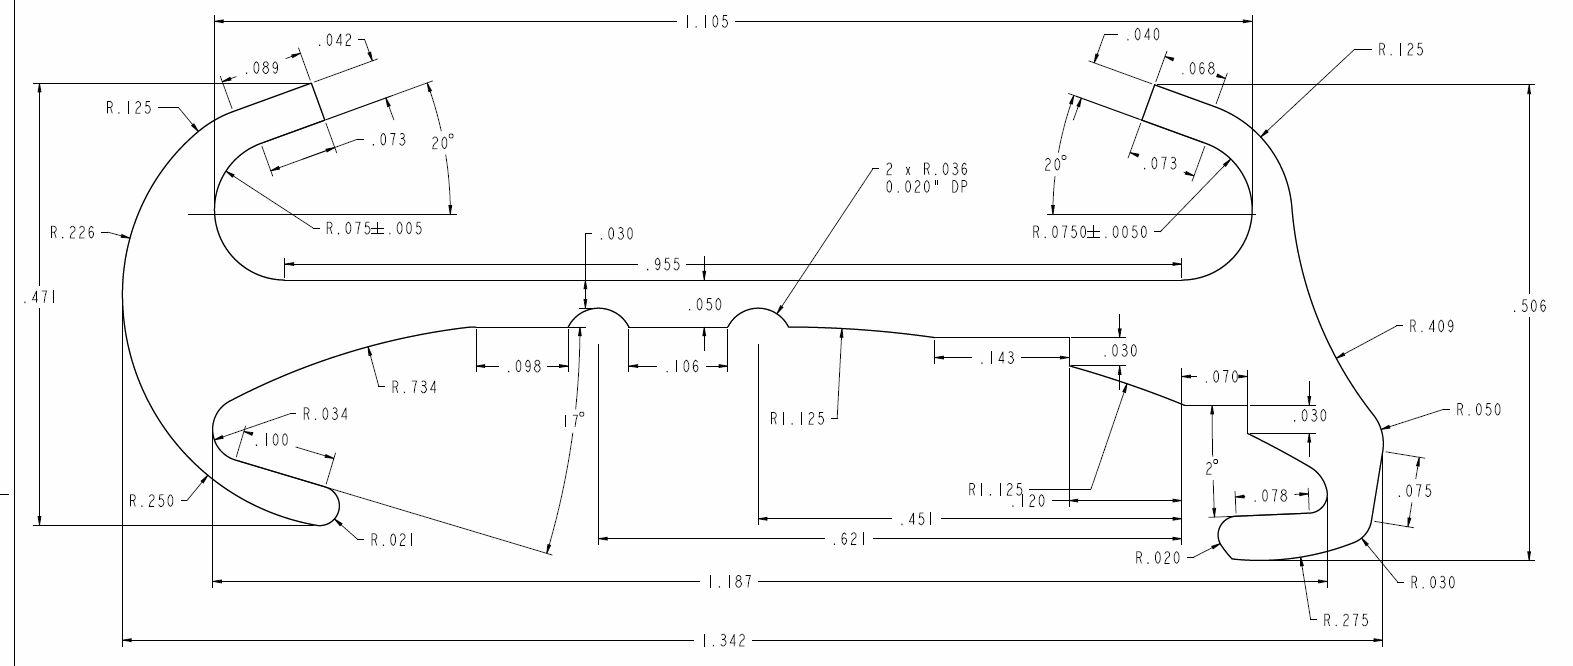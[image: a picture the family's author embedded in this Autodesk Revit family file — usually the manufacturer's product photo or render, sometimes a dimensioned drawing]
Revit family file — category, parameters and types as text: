
# Revit family: ONRZH 5.125'' Heated only-All
name_source: partatom
category: Mechanical Equipment
units: mm (PartAtom-declared; Revit-internal decimal feet)

## family parameters
Always vertical = Yes
Cut with Voids When Loaded = No
OmniClass Number = 23.40.40.11.17
OmniClass Title = Refrigerated Cases
Part Type = Normal
Room Calculation Point = No
Round Connector Dimension = Use Radius
Shared = No
Work Plane-Based = Yes

## types (6) — shared parameters
22" Shelf = Yes
ANTI CON AMPS = 4 A
BASE = BLACK
Certifications = NSF 7, UL471, CSA
DATE = 02/08/2016
DEFROST AMPS = 26 A
DESIGNERS NAME = SHIDDRAMESH
DISCHARGE AIR TEMP. = -8 °F
DISCHARGE AIR VELOCITY = 350 FPM
DRAIN HEATERS AMPS = 3 A
Default Elevation = 48"
Defrost Num Day = 4
Defrost Termination = 50 °F
Defrost Type = ELECTRIC DEFROST
Defrosts Per Day_2 = 1
Description = High Narrow Back-to-Back Reach-In Glass Door Merchandiser
Discharge Air Velocity (FPM) = 350
Door Type = Heated
EQUIPMENT DESCRIPTION = High Narrow Back-to-Back Reach-In Glass Door Merchandiser
EQUIPMENT MARK = ONRZH
Electric Defrost Fail-Safe = 46
Electric Defrost Run-Off Time (Min) = 0
Electric Defrost Termination = 50
Evap Temp = -15
HIGH EFFICIENCY FANS AMPS = 1 A
Height = 85 1/4"
Hot Gas Defrost Fail-Safe = 24
Hot Gas Defrost Run-Off Time (Min) = 13-15
Hot Gas Defrost Termination = 73
Item Description = High Narrow Back-to-Back Reach-In Glass Door Merchandiser
LIGHT AMPS = 1 A
Legend Number = ONRZH
Load Mbh = 1.06
Manufacturer = HILL PHOENIX
Model = ONRZH
POWER FACTOR = 1
Painted Metal Exterior = CHARCOAL BROWN
REFRIGERATION PIPING = COPPER PIPE
Refrig Charge Lbs = 0
Superheat Set Point @ Bulb (F) = 3-5
URL = http://www.hillphoenix.com
Width = 67 1/8"
length = Yes

## per-type parameters (varying)
- 2- Door Frozen Food: 101-LE DOOR FRAME AMPS=1 A; 101-LE DOOR FRAME WATTS=151 W; 208 Amps SSD Defrost Phase 1=7.5; 208 Watts SSD Defrost Phase 1=1552; 240 Amps SSD Defrost  Phase 1=8.6; 240 Watts SSD Defrost Phase 1=2068; 3 Phase SSD Defrost 208 Amps=6.5; 3 Phase SSD Defrost 208 Watts=1552; 3 Phase SSD Defrost 240 Amps=7.5; 3 Phase SSD Defrost 240 Watts=2068; Application Discipline=Frozen; BTUH Conventional=910; BTUH Parallel=895; CENTER LINE & DRAIN=30"; DOOR CONFIGURATION=MASTER DOOR : 30" X 68 3/8" 2 DOOR A SWING (LEFT OPENING); Discharge Air (F)=-1; Evaportator (F)=-7; GE Immersion Amps=0 A; GE Immersion Watts=41 W; Heated Doors Amps=0.78; Heated Doors Watts=67; Heated Option Amps=2.04; Heated Option Watts=219; Length=60"; Low E Doors Amps=0.34; Low E Doors Watts=41; Low E Rails Amps=1.6; Low E Rails Watts=192; Optimax Pro Amps=0 A; Optimax Pro Watts=43 W; SSD Fans Per Case=2; SSD High Efficiency Amps=0.6; SSD High Efficiency Fan Watts=50; SSD Tank Heater Amps=1.6; SSD Tank Heater Watts=152
- 3-Door Frozen Food: 101-LE DOOR FRAME AMPS=2 A; 101-LE DOOR FRAME WATTS=211 W; 208 Amps SSD Defrost Phase 1=10.9; 208 Watts SSD Defrost Phase 1=2274; 240 Amps SSD Defrost  Phase 1=12.6; 240 Watts SSD Defrost Phase 1=3018; 3 Phase SSD Defrost 208 Amps=9.5; 3 Phase SSD Defrost 208 Watts=2274; 3 Phase SSD Defrost 240 Amps=10.9; 3 Phase SSD Defrost 240 Watts=3018; Application Discipline=Ice Cream; BTUH Conventional=1017; BTUH Parallel=996; CENTER LINE & DRAIN=45"; DOOR CONFIGURATION=MASTER DOOR : 30" X 68 3/8" 3 DOOR A SWING (LEFT OPENING); Discharge Air (F)=-8; Evaportator (F)=-15; GE Immersion Amps=0 A; GE Immersion Watts=48 W; Heated Doors Amps=1.17; Heated Doors Watts=101; Heated Option Amps=2.93; Heated Option Watts=312; Length=90"; Low E Doors Amps=0.51; Low E Doors Watts=61; Low E Rails Amps=2.27; Low E Rails Watts=272; Optimax Pro Amps=1 A; Optimax Pro Watts=65 W; SSD Fans Per Case=3; SSD High Efficiency Amps=1; SSD High Efficiency Fan Watts=75; SSD Tank Heater Amps=1.5; SSD Tank Heater Watts=171
- 4-Door Frozen Food: 101-LE DOOR FRAME AMPS=2 A; 101-LE DOOR FRAME WATTS=275 W; 208 Amps SSD Defrost Phase 1=14.3; 208 Watts SSD Defrost Phase 1=2984; 240 Amps SSD Defrost  Phase 1=16.6; 240 Watts SSD Defrost Phase 1=3992; 3 Phase SSD Defrost 208 Amps=12.4; 3 Phase SSD Defrost 208 Watts=2984; 3 Phase SSD Defrost 240 Amps=14.4; 3 Phase SSD Defrost 240 Watts=3992; Application Discipline=Ice Cream; BTUH Conventional=910; BTUH Parallel=895; CENTER LINE & DRAIN=60"; DOOR CONFIGURATION=MASTER DOOR : 30" X 68 3/8" 4 DOOR A SWING (LEFT OPENING); Discharge Air (F)=-1; Evaportator (F)=-7; GE Immersion Amps=1 A; GE Immersion Watts=64 W; Heated Doors Amps=1.56; Heated Doors Watts=135; Heated Option Amps=3.85; Heated Option Watts=410; Length=120"; Low E Doors Amps=0.68; Low E Doors Watts=82; Low E Rails Amps=2.97; Low E Rails Watts=356; Optimax Pro Amps=1 A; Optimax Pro Watts=87 W; SSD Fans Per Case=4; SSD High Efficiency Amps=1.3; SSD High Efficiency Fan Watts=100; SSD Tank Heater Amps=1.9; SSD Tank Heater Watts=226
- 5-Door Frozen Food: 101-LE DOOR FRAME AMPS=3 A; 101-LE DOOR FRAME WATTS=334 W; 208 Amps SSD Defrost Phase 1=17.5; 208 Watts SSD Defrost Phase 1=3640; 240 Amps SSD Defrost  Phase 1=20.2; 240 Watts SSD Defrost Phase 1=4840; 3 Phase SSD Defrost 208 Amps=15.1; 3 Phase SSD Defrost 208 Watts=3640; 3 Phase SSD Defrost 240 Amps=17.4; 3 Phase SSD Defrost 240 Watts=4840; Application Discipline=Ice Cream; BTUH Conventional=910; BTUH Parallel=895; CENTER LINE & DRAIN=75"; DOOR CONFIGURATION=MASTER DOOR : 30" X 68 3/8" 5 DOOR A SWING (LEFT OPENING); Discharge Air (F)=-1; Evaportator (F)=-7; GE Immersion Amps=1 A; GE Immersion Watts=80 W; Heated Doors Amps=1.95; Heated Doors Watts=168; Heated Option Amps=4.73; Heated Option Watts=502; Length=150"; Low E Doors Amps=0.85; Low E Doors Watts=101; Low E Rails Amps=3.63; Low E Rails Watts=436; Optimax Pro Amps=1 A; Optimax Pro Watts=109 W; SSD Fans Per Case=5; SSD High Efficiency Amps=1.6; SSD High Efficiency Fan Watts=125; SSD Tank Heater Amps=2.3; SSD Tank Heater Watts=275
- 6-Door Frozen Food: 101-LE DOOR FRAME AMPS=3 A; 101-LE DOOR FRAME WATTS=394 W; 208 Amps SSD Defrost Phase 1=20.3; 208 Watts SSD Defrost Phase 1=4224; 240 Amps SSD Defrost  Phase 1=23.4; 240 Watts SSD Defrost Phase 1=5624; 3 Phase SSD Defrost 208 Amps=17.6; 3 Phase SSD Defrost 208 Watts=4224; 3 Phase SSD Defrost 240 Amps=20.3; 3 Phase SSD Defrost 240 Watts=5624; Application Discipline=Frozen Food; BTUH Conventional=910; BTUH Parallel=895; CENTER LINE & DRAIN=90"; DOOR CONFIGURATION=MASTER DOOR : 30" X 68 3/8" 6 DOOR A SWING (LEFT OPENING); Discharge Air (F)=-1; Evaportator (F)=-7; GE Immersion Amps=1 A; GE Immersion Watts=96 W; Heated Doors Amps=2.34; Heated Doors Watts=201; Heated Option Amps=5.62; Heated Option Watts=596; Length=180"; Low E Doors Amps=1.02; Low E Doors Watts=122; Low E Rails Amps=4.3; Low E Rails Watts=516; Optimax Pro Amps=1 A; Optimax Pro Watts=132 W; SSD Fans Per Case=6; SSD High Efficiency Amps=1.9; SSD High Efficiency Fan Watts=150; SSD Tank Heater Amps=2.7; SSD Tank Heater Watts=320
- 1- Door Frozen Food: 101-LE DOOR FRAME AMPS=1 A; 101-LE DOOR FRAME WATTS=91 W; 208 Amps SSD Defrost Phase 1=3.27; 208 Watts SSD Defrost Phase 1=680; 240 Amps SSD Defrost  Phase 1=3.78; 240 Watts SSD Defrost Phase 1=906; 3 Phase SSD Defrost 208 Amps=2.85; 3 Phase SSD Defrost 208 Watts=680; 3 Phase SSD Defrost 240 Amps=3.31; 3 Phase SSD Defrost 240 Watts=906; Application Discipline=Frozen; BTUH Conventional=910; BTUH Parallel=895; CENTER LINE & DRAIN=15 1/2"; DOOR CONFIGURATION=MASTER DOOR.0002 : 31" X 68 3/8" 1 DOOR A SWING (LEFT OPENING); Discharge Air (F)=-1; Evaportator (F)=-7; GE Immersion Amps=0 A; GE Immersion Watts=27 W; Heated Doors Amps=0.39; Heated Doors Watts=34; Heated Option Amps=1.15; Heated Option Watts=125; Length=31"; Low E Doors Amps=0.17; Low E Doors Watts=21; Low E Rails Amps=0.93; Low E Rails Watts=112; Optimax Pro Amps=0 A; Optimax Pro Watts=21 W; SSD Fans Per Case=1; SSD High Efficiency Amps=0.3; SSD High Efficiency Fan Watts=25; SSD Tank Heater Amps=0.09; SSD Tank Heater Watts=113

## geometry (parser evidence)
native form markers: Blend x10, Sweep x32
no freeform markers — native parametric forms only
